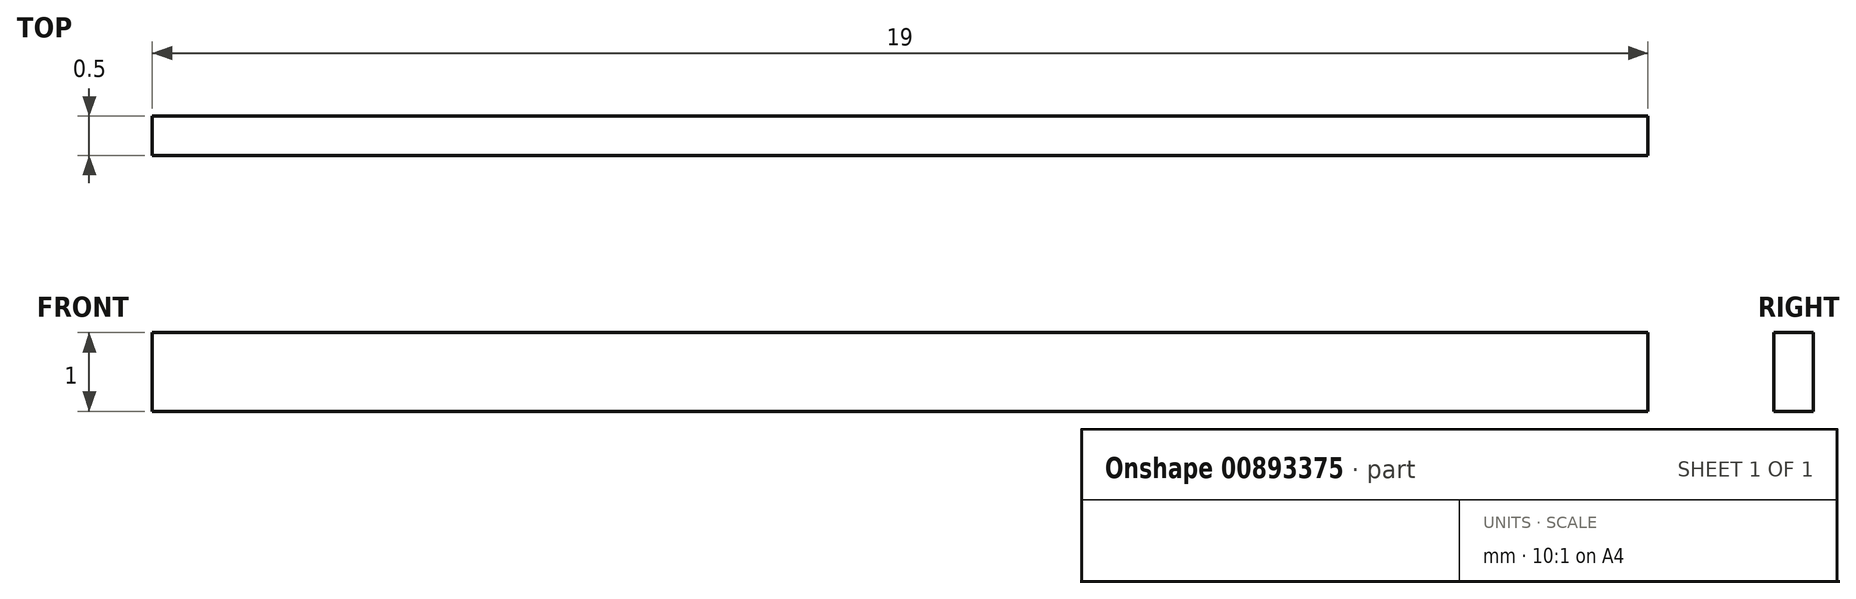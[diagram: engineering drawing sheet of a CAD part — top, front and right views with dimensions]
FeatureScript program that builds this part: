
annotation { "Feature Type Name" : "Feature", "Feature Type Description" : "" }
export const myFeature = defineFeature(function(context is Context, id is Id, definition is map)
    precondition{}
    {
        {
            var Q0;
            Q0=qCreatedBy(makeId("Front.planeOp"),FACE);
            var sketch = newSketch(context, id + "F0", { "sketchPlane" : qUnion([Q0])});
            skLineSegment(sketch, "E0.bottom", {"start": v(9.5, 0.5) * mm, "end": v(-9.5, 0.5) * mm});
            skLineSegment(sketch, "E0.top", {"start": v(9.5, -0.5) * mm, "end": v(-9.5, -0.5) * mm});
            skLineSegment(sketch, "E0.left", {"start": v(9.5, 0.5) * mm, "end": v(9.5, -0.5) * mm});
            skLineSegment(sketch, "E0.right", {"start": v(-9.5, 0.5) * mm, "end": v(-9.5, -0.5) * mm});
            skPoint(sketch, "E0.middle", {"position": v(0, 0) * mm});
            skSolve(sketch);
        }
        {
            var Q0;
            Q0 = qSketchRegion(id + "F0", true);
            extrude(context, id + "F1", {"entities" : qUnion([Q0]), "depth" : 0.5 * mm, "offsetDistance" : 25 * mm});
        }
    });
